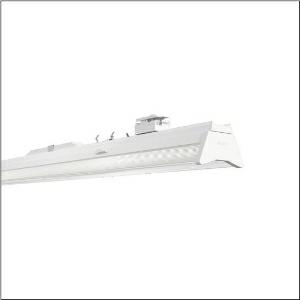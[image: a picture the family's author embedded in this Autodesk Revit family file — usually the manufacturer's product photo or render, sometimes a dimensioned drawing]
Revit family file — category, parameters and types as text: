
# Revit family: licross_r__21_performance_mo_52td16vn465g_2158
name_source: partatom
category: Lighting Fixtures
units: mm (PartAtom-declared; Revit-internal decimal feet)

## family parameters
Cut with Voids When Loaded = No
Host = Face
Light Source = No
Part Type = Normal
Room Calculation Point = No
Round Connector Dimension = Use Diameter
Shared = No

## types (1)
- --- (1 x LED, 6500 lm, 36.1 W, 4000K)
    Apparent Load = 36 VA
    CIE Flux Codes = 66 88 96 79 100
    Color Rendering = 80
    Color Temperature = 4000K
    Default Elevation = 1800 mm
    Description = Licross® 21 Performance MO, luminaire insert, of sheet steel, galvanised, coil coated, white, length: 1.500mm, width: 120mm, height: 123mm, LED rated luminous flux: 6.500lm, light colour: 840, control gear: DALI 2, CLO, with plug, 5-pole, with phase selection, mains connection: 220..240V, AC, 50/60Hz, start of lifetime: 36W, end of service life: 43W, internal wiring halogen-free, primary light control with lens, of plastic, primary optical cover: cover, of PMMA, light emission: direct/indirect distribution, primary light characteristic: symmetric, protection rating (complete): IP54, insulation class (complete): insulation class I (protective earthing), certification: CE, ENEC, VDE, UKCA, protection symbol: D if used in an environment with non-conductive dust loads with corresponding accessories, impact resistance: IK06, permissible ambient temperature for indoor applications: -25..+45°C, corresponds to IFS (International Featured Standards) requirements for safety and quality in the food industry, reducing of maximum allowable ambient temperature of 5°C with ceiling mounting, LABS conformity tested according to VDMA 24364:2018-05, packaging unit: 1 piece
    Height = 114 mm
    Lamp = 1 x LED
    Lamp Light Flux = 6500 lm
    Lamp Power = 36.1 W
    Lamp count = 1
    Length = 1500 mm
    Luminous efficacy = 180 lm/W
    Manufacturer = Siteco
    ModVariant = No
    Model = 52TD16VN465G
    Mounting Place = Ceiling
    Mounting Type = Pendant
    Number of Poles = 1
    OnlyDefault = Yes
    Power Factor = 1
    Product Name = Licross® 21 Performance MO
    Product group = luminaire insert | ceiling pendant
    ProductGroupID = 902
    Protection Class = Protection class I
    Protection Degree = IP 54
    RLX_Detail_Level = 1
    RLX_Emergency_Light_Flux = 0 lm
    RLX_Emergency_Type = 0
    RLX_Emergency_Type_DB = No
    RlxData = <blob elided: 34041 chars, md5=fdaa6582>
    Socket = socket
    Standby Power = 0 W
    System Light Flux = 6500 lm
    System Power = 36 W
    Type Comments = factory setting: luminous flux: 100 % | dim-lin: 254 | 242 mA
    Type Image = l_1256138.jpg
    URL = http://relux.com
    VarID = @adj_104501
    Voltage = 0 V
    Weight = 0.00 kg
    Width = 120 mm

## geometry (parser evidence)
native form markers: Blend x4, Sweep x13
no freeform markers — native parametric forms only
